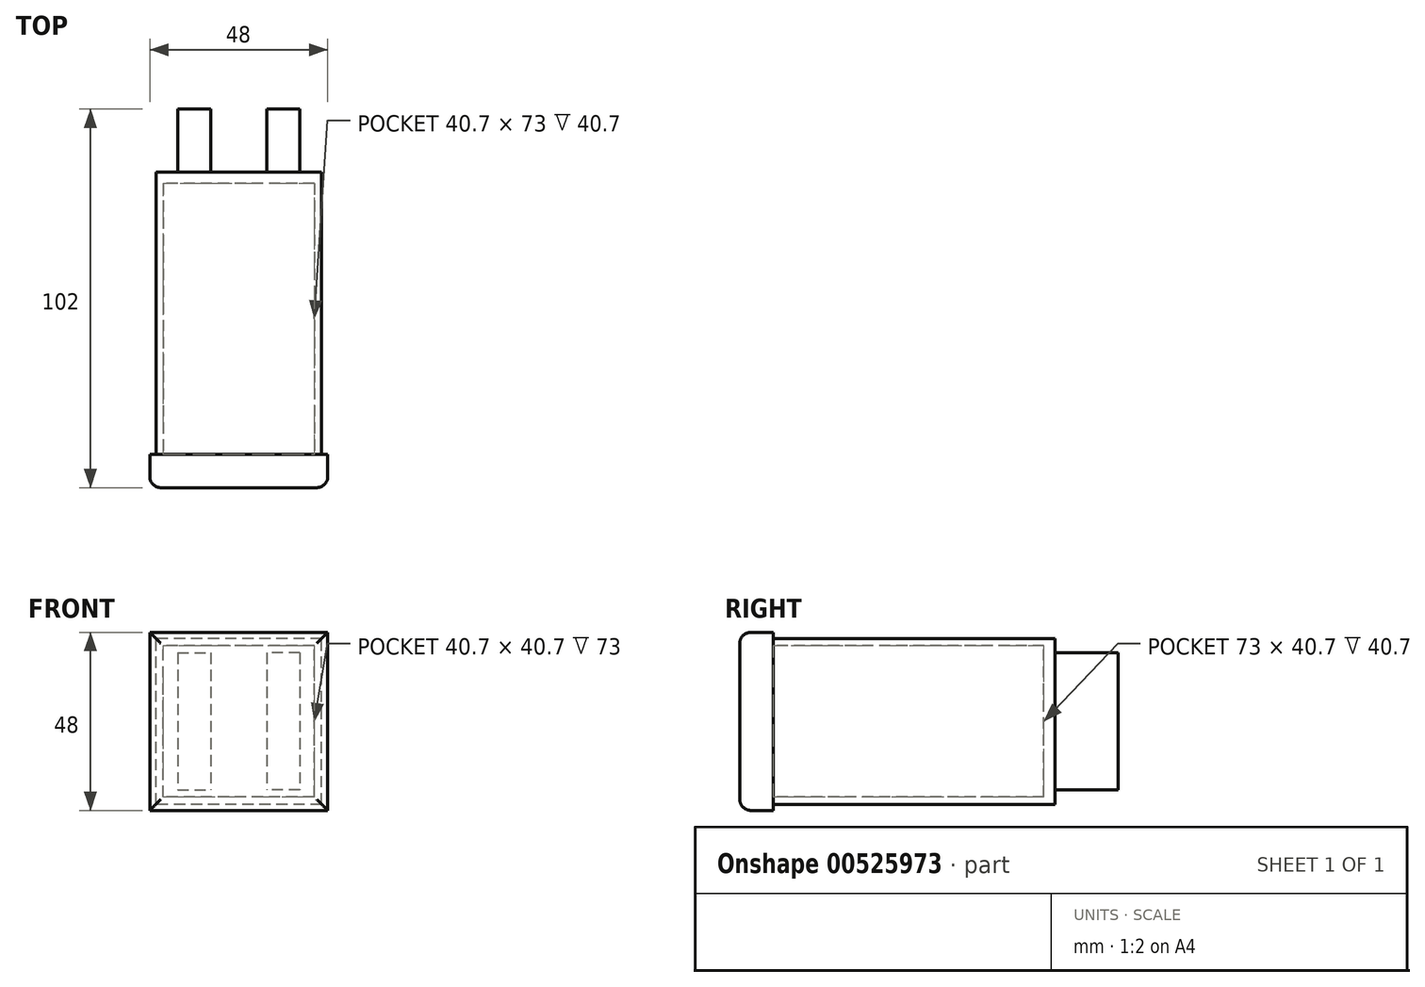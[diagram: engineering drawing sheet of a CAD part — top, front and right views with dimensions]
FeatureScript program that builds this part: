
annotation { "Feature Type Name" : "Feature", "Feature Type Description" : "" }
export const myFeature = defineFeature(function(context is Context, id is Id, definition is map)
    precondition{}
    {
        {
            var Q0;
            Q0=qCreatedBy(makeId("Front.planeOp"),FACE);
            var sketch = newSketch(context, id + "F0", { "sketchPlane" : qUnion([Q0])});
            skLineSegment(sketch, "E0.bottom", {"start": v(22.35, -22.35) * mm, "end": v(-22.35, -22.35) * mm});
            skLineSegment(sketch, "E0.top", {"start": v(22.35, 22.35) * mm, "end": v(-22.35, 22.35) * mm});
            skLineSegment(sketch, "E0.left", {"start": v(22.35, -22.35) * mm, "end": v(22.35, 22.35) * mm});
            skLineSegment(sketch, "E0.right", {"start": v(-22.35, -22.35) * mm, "end": v(-22.35, 22.35) * mm});
            skPoint(sketch, "E0.middle", {"position": v(0, 0) * mm});
            skLineSegment(sketch, "E1.0", {"start": v(20.35, 20.35) * mm, "end": v(-20.35, 20.35) * mm});
            skLineSegment(sketch, "E1.1", {"start": v(20.35, -20.35) * mm, "end": v(20.35, 20.35) * mm});
            skLineSegment(sketch, "E1.2", {"start": v(20.35, -20.35) * mm, "end": v(-20.35, -20.35) * mm});
            skLineSegment(sketch, "E1.3", {"start": v(-20.35, -20.35) * mm, "end": v(-20.35, 20.35) * mm});
            skLineSegment(sketch, "E2.bottom", {"start": v(24, 24) * mm, "end": v(-24, 24) * mm});
            skLineSegment(sketch, "E2.top", {"start": v(24, -24) * mm, "end": v(-24, -24) * mm});
            skLineSegment(sketch, "E2.left", {"start": v(24, 24) * mm, "end": v(24, -24) * mm});
            skLineSegment(sketch, "E2.right", {"start": v(-24, 24) * mm, "end": v(-24, -24) * mm});
            skSolve(sketch);
        }
        {
            var Q0;
            Q0=makeQuery(id+"F0.imprint","IMPRINT",FACE,{"disambiguationData":[TD([[makeQuery(id+"F0.imprint","IMPRINT",EDGE,{"derivedFrom":sQuery(id+"F0.wireOp",EDGE,"E0.bottom")}),-1.0]])]});
            extrude(context, id + "F1", {"entities" : qUnion([Q0]), "oppositeDirection" : true, "depth" : 73 * mm, "offsetDistance" : 25 * mm});
        }
        {
            var Q0;
            Q0=makeQuery(id+"F1.opExtrude","CAP_FACE",FACE,{"disambiguationData":[OSD([sQuery(id+"F0.wireOp",EDGE,"E0.bottom"),sQuery(id+"F0.wireOp",EDGE,"E0.top"),sQuery(id+"F0.wireOp",EDGE,"E0.left"),sQuery(id+"F0.wireOp",EDGE,"E0.right"),sQuery(id+"F0.wireOp",EDGE,"E1.0"),sQuery(id+"F0.wireOp",EDGE,"E1.1"),sQuery(id+"F0.wireOp",EDGE,"E1.2"),sQuery(id+"F0.wireOp",EDGE,"E1.3")])],"isStart":false});
            var sketch = newSketch(context, id + "F2", { "sketchPlane" : qUnion([Q0])});
            skLineSegment(sketch, "E3.bottom", {"start": v(-16.5, 18.5) * mm, "end": v(-7.5, 18.5) * mm});
            skLineSegment(sketch, "E3.top", {"start": v(-16.5, -18.5) * mm, "end": v(-7.5, -18.5) * mm});
            skLineSegment(sketch, "E3.left", {"start": v(-16.5, 18.5) * mm, "end": v(-16.5, -18.5) * mm});
            skLineSegment(sketch, "E3.right", {"start": v(-7.5, 18.5) * mm, "end": v(-7.5, -18.5) * mm});
            skPoint(sketch, "E3.middle", {"position": v(-12, 0) * mm});
            skLineSegment(sketch, "E4.MirrorCS", {"start": v(7.5, 18.5) * mm, "end": v(7.5, -18.5) * mm});
            skLineSegment(sketch, "E5.MirrorCS", {"start": v(16.5, 18.5) * mm, "end": v(16.5, -18.5) * mm});
            skLineSegment(sketch, "E6.MirrorCS", {"start": v(16.5, -18.5) * mm, "end": v(7.5, -18.5) * mm});
            skLineSegment(sketch, "E7.MirrorCS", {"start": v(16.5, 18.5) * mm, "end": v(7.5, 18.5) * mm});
            skPoint(sketch, "E8.MirrorP", {"position": v(12, 0) * mm});
            skSolve(sketch);
        }
        {
            var Q0;
            Q0=makeQuery(id+"F2.imprint","IMPRINT",FACE,{"disambiguationData":[TD([[makeQuery(id+"F2.imprint","IMPRINT",EDGE,{"derivedFrom":sQuery(id+"F2.wireOp",EDGE,"E3.bottom")}),1.0]])]});
            var Q1;
            Q1=makeQuery(id+"F2.imprint","IMPRINT",FACE,{"disambiguationData":[TD([[makeQuery(id+"F2.imprint","IMPRINT",EDGE,{"derivedFrom":makeQuery(id+"F1.opExtrude","CAP_EDGE",EDGE,{"disambiguationData":[OSD([sQuery(id+"F0.wireOp",EDGE,"E0.bottom")])],"isStart":false})}),1.0]])]});
            extrude(context, id + "F3", {"entities" : qUnion([Q0, Q1]), "operationType" : NewBodyOperationType.ADD, "depth" : 3 * mm, "offsetDistance" : 25 * mm});
        }
        {
            var Q0;
            Q0=makeQuery(id+"F2.imprint","IMPRINT",FACE,{"disambiguationData":[TD([[makeQuery(id+"F2.imprint","IMPRINT",EDGE,{"derivedFrom":sQuery(id+"F2.wireOp",EDGE,"E3.bottom")}),-1.0]])]});
            var Q1;
            Q1=makeQuery(id+"F2.imprint","IMPRINT",FACE,{"disambiguationData":[TD([[makeQuery(id+"F2.imprint","IMPRINT",EDGE,{"derivedFrom":sQuery(id+"F2.wireOp",EDGE,"E4.MirrorCS")}),1.0]])]});
            extrude(context, id + "F4", {"entities" : qUnion([Q0, Q1]), "operationType" : NewBodyOperationType.ADD, "depth" : 20 * mm, "offsetDistance" : 25 * mm});
        }
        {
            var Q0;
            Q0=makeQuery(id+"F0.imprint","IMPRINT",FACE,{"disambiguationData":[TD([[makeQuery(id+"F0.imprint","IMPRINT",EDGE,{"derivedFrom":sQuery(id+"F0.wireOp",EDGE,"E0.bottom")}),1.0]])]});
            var Q1;
            Q1=makeQuery(id+"F0.imprint","IMPRINT",FACE,{"disambiguationData":[TD([[makeQuery(id+"F0.imprint","IMPRINT",EDGE,{"derivedFrom":sQuery(id+"F0.wireOp",EDGE,"E0.bottom")}),-1.0]])]});
            var Q2;
            Q2=makeQuery(id+"F0.imprint","IMPRINT",FACE,{"disambiguationData":[TD([[makeQuery(id+"F0.imprint","IMPRINT",EDGE,{"derivedFrom":sQuery(id+"F0.wireOp",EDGE,"E1.0")}),1.0]])]});
            extrude(context, id + "F5", {"entities" : qUnion([Q0, Q1, Q2]), "operationType" : NewBodyOperationType.ADD, "depth" : 9 * mm, "offsetDistance" : 25 * mm});
        }
        {
            var Q0;
            Q0=makeQuery(id+"F5.opExtrude","CAP_FACE",FACE,{"disambiguationData":[OSD([sQuery(id+"F0.wireOp",EDGE,"E2.bottom"),sQuery(id+"F0.wireOp",EDGE,"E2.top"),sQuery(id+"F0.wireOp",EDGE,"E2.left"),sQuery(id+"F0.wireOp",EDGE,"E2.right")])],"isStart":false});
            fillet(context, id + "F6", {"entities" : qUnion([Q0]), "radius" : 3 * mm, "tangentPropagation" : true, "allowEdgeOverflow" : false});
        }
    });
